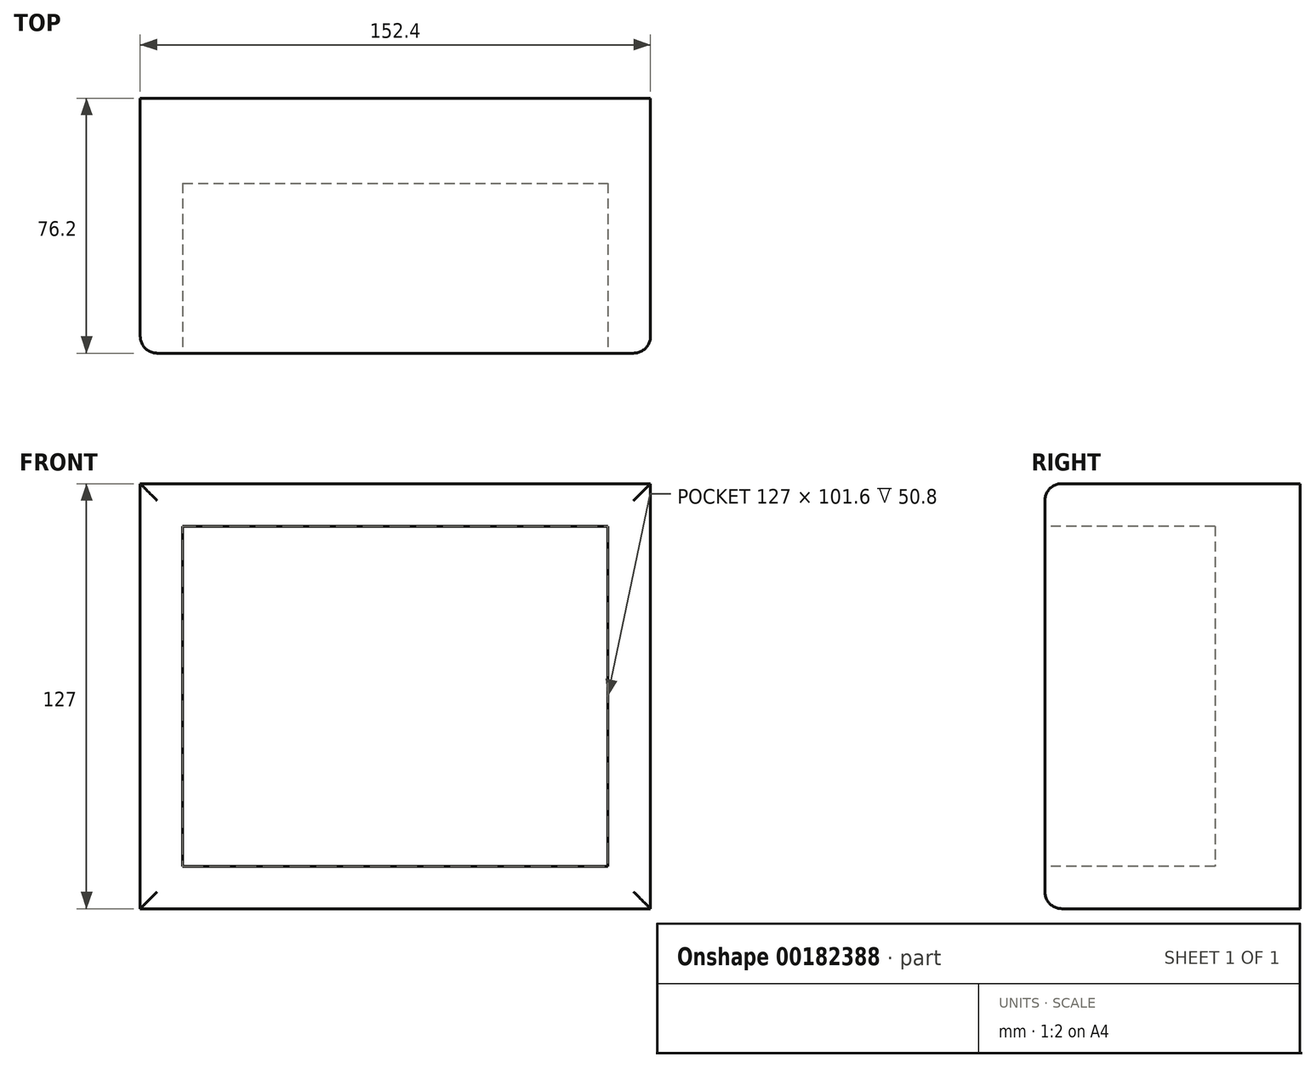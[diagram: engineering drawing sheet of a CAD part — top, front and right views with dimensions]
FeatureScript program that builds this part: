
annotation { "Feature Type Name" : "Feature", "Feature Type Description" : "" }
export const myFeature = defineFeature(function(context is Context, id is Id, definition is map)
    precondition{}
    {
        {
            var Q0;
            Q0=qCreatedBy(makeId("Front.planeOp"),FACE);
            var sketch = newSketch(context, id + "F0", { "sketchPlane" : qUnion([Q0])});
            skLineSegment(sketch, "E0.bottom", {"start": v(-76.2, 63.5) * mm, "end": v(76.2, 63.5) * mm});
            skLineSegment(sketch, "E0.top", {"start": v(-76.2, -63.5) * mm, "end": v(76.2, -63.5) * mm});
            skLineSegment(sketch, "E0.left", {"start": v(-76.2, 63.5) * mm, "end": v(-76.2, -63.5) * mm});
            skLineSegment(sketch, "E0.right", {"start": v(76.2, 63.5) * mm, "end": v(76.2, -63.5) * mm});
            skPoint(sketch, "E0.middle", {"position": v(0, 0) * mm});
            skSolve(sketch);
        }
        {
            var Q0;
            Q0=makeQuery(id+"F0.imprint","IMPRINT",FACE,{"disambiguationData":[TD([[makeQuery(id+"F0.imprint","IMPRINT",EDGE,{"derivedFrom":sQuery(id+"F0.wireOp",EDGE,"E0.bottom")}),-1.0]])]});
            extrude(context, id + "F1", {"entities" : qUnion([Q0]), "oppositeDirection" : true, "depth" : 76.2 * mm});
        }
        {
            var Q0;
            Q0=makeQuery(id+"F1.opExtrude","CAP_FACE",FACE,{"disambiguationData":[OSD([sQuery(id+"F0.wireOp",EDGE,"E0.bottom"),sQuery(id+"F0.wireOp",EDGE,"E0.top"),sQuery(id+"F0.wireOp",EDGE,"E0.left"),sQuery(id+"F0.wireOp",EDGE,"E0.right")])],"isStart":true});
            var sketch = newSketch(context, id + "F2", { "sketchPlane" : qUnion([Q0])});
            skLineSegment(sketch, "E1.bottom", {"start": v(-63.5, 50.8) * mm, "end": v(63.5, 50.8) * mm});
            skLineSegment(sketch, "E1.top", {"start": v(-63.5, -50.8) * mm, "end": v(63.5, -50.8) * mm});
            skLineSegment(sketch, "E1.left", {"start": v(-63.5, 50.8) * mm, "end": v(-63.5, -50.8) * mm});
            skLineSegment(sketch, "E1.right", {"start": v(63.5, 50.8) * mm, "end": v(63.5, -50.8) * mm});
            skPoint(sketch, "E1.middle", {"position": v(0, 0) * mm});
            skSolve(sketch);
        }
        {
            var Q0;
            Q0=makeQuery(id+"F2.imprint","IMPRINT",FACE,{"disambiguationData":[TD([[makeQuery(id+"F2.imprint","IMPRINT",EDGE,{"derivedFrom":sQuery(id+"F2.wireOp",EDGE,"E1.bottom")}),-1.0]])]});
            extrude(context, id + "F3", {"entities" : qUnion([Q0]), "operationType" : NewBodyOperationType.REMOVE, "oppositeDirection" : true, "depth" : 50.8 * mm});
        }
        {
            var Q0;
            Q0=makeQuery(id+"F3.boolean.opBoolean","COPY",EDGE,{"derivedFrom":makeQuery(id+"F3.opExtrude","CAP_EDGE",EDGE,{"disambiguationData":[OSD([sQuery(id+"F2.wireOp",EDGE,"E1.bottom")])],"isStart":true})});
            var Q1;
            Q1=makeQuery(id+"F1.opExtrude","CAP_EDGE",EDGE,{"disambiguationData":[OSD([sQuery(id+"F0.wireOp",EDGE,"E0.bottom")])],"isStart":true});
            var Q2;
            Q2=makeQuery(id+"F3.boolean.opBoolean","COPY",EDGE,{"derivedFrom":makeQuery(id+"F3.opExtrude","CAP_EDGE",EDGE,{"disambiguationData":[OSD([sQuery(id+"F2.wireOp",EDGE,"E1.right")])],"isStart":true})});
            var Q3;
            Q3=makeQuery(id+"F3.boolean.opBoolean","COPY",EDGE,{"derivedFrom":makeQuery(id+"F3.opExtrude","CAP_EDGE",EDGE,{"disambiguationData":[OSD([sQuery(id+"F2.wireOp",EDGE,"E1.top")])],"isStart":true})});
            var Q4;
            Q4=makeQuery(id+"F3.boolean.opBoolean","COPY",EDGE,{"derivedFrom":makeQuery(id+"F3.opExtrude","CAP_EDGE",EDGE,{"disambiguationData":[OSD([sQuery(id+"F2.wireOp",EDGE,"E1.left")])],"isStart":true})});
            var Q5;
            Q5=makeQuery(id+"F1.opExtrude","CAP_EDGE",EDGE,{"disambiguationData":[OSD([sQuery(id+"F0.wireOp",EDGE,"E0.left")])],"isStart":true});
            var Q6;
            Q6=makeQuery(id+"F1.opExtrude","CAP_EDGE",EDGE,{"disambiguationData":[OSD([sQuery(id+"F0.wireOp",EDGE,"E0.top")])],"isStart":true});
            var Q7;
            Q7=makeQuery(id+"F1.opExtrude","CAP_EDGE",EDGE,{"disambiguationData":[OSD([sQuery(id+"F0.wireOp",EDGE,"E0.right")])],"isStart":true});
            fillet(context, id + "F4", {"entities" : qUnion([Q0, Q1, Q2, Q3, Q4, Q5, Q6, Q7]), "radius" : 5.08 * mm, "tangentPropagation" : true, "allowEdgeOverflow" : false});
        }
    });
